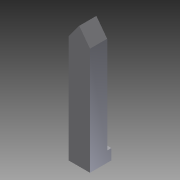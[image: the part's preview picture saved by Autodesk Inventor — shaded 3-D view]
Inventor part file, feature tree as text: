
AUTODESK INVENTOR PART (.ipt)
format: ipt  version: 2012 (Build 160160000, 160)  size: 75,776 bytes
history: native  units: in
note: dims shown in document units (in); Inventor stores cm internally (conversion verified against a paired STEP export)
features: extrude x2, sketch x2
ambient origin geometry x8: Origin, YZ Plane, XZ Plane, XY Plane, X Axis, Y Axis, Z Axis, Center Point
bodies: Solid1 (feature_tree)
feature tree (4):
  extrude  "Extrusion1"  Depth=0.05in TaperAngle=0.0deg
  extrude  "Extrusion2"  [1 undecoded]
  sketch  "Sketch1"  dims[d2=0.2in d3=0.0in d4=0.05in d5=0.0in]
  sketch  "Sketch2"
note: 1 required parameter value undecoded (feature->parameter linkage not recoverable at this tier; creation-order binding heuristic only, values carry confidence <= 0.55)
